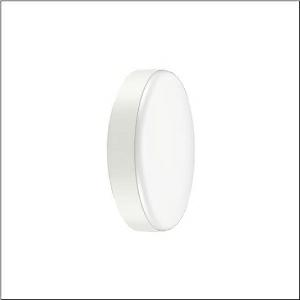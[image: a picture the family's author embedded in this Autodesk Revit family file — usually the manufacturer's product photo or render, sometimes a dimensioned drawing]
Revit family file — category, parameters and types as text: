
# Revit family: round_31_51wc10db44as
name_source: partatom
category: Lighting Fixtures
units: mm (PartAtom-declared; Revit-internal decimal feet)

## family parameters
Cut with Voids When Loaded = No
Host = Face
Light Source = No
Part Type = Normal
Room Calculation Point = No
Round Connector Dimension = Use Diameter
Shared = No

## types (1)
- Round 31 (1 x LED, 4400 lm, 35.5 W, 4000K)
    Apparent Load = 36 VA
    CIE Flux Codes = 44 75 94 94 100
    Color Rendering = 80
    Color Temperature = 4000K
    Default Elevation = 1800 mm
    Description = Round 31, wall and ceiling luminaire, primary optical cover: cover, of PC, opal, light emission: direct distribution, primary light characteristic: symmetric, installation type: surface-mounted, LED, rated luminous flux: 4.400lm, luminous efficacy: 124lm/W, light colour: 840, colour temperature: 4000K, control gear: DALI 2, with terminal, 3-pole, max. 2.5mm², mains connection: 220..240V, AC, 50/60Hz, rated input power: 35.5W, luminaire housing, of PC, traffic white (RAL 9016), diameter: 480mm, brightness and presence sensor, HF sensor, protection rating (complete): IP65, insulation class (complete): insulation class II (safety insulation), certification: CE, impact resistance: IK10, permissible operating ambient temperature: -20..+40°C, permissible storage temperature: -20..+60°C, packaging unit: 1 piece
    Height = 97 mm
    Lamp = 1 x LED
    Lamp Light Flux = 4400 lm
    Lamp Power = 35.5 W
    Lamp count = 1
    Length = 480 mm
    Luminous efficacy = 124 lm/W
    Manufacturer = Siteco
    ModVariant = No
    Model = 51WC10DB44AS
    Mounting Place = Ceiling
    Mounting Type = Surface mounted
    Number of Poles = 1
    OnlyDefault = Yes
    Power Factor = 1
    Product Name = Round 31
    Product group = wall and ceiling luminaire | ceiling mounted
    ProductGroupID = 305
    Protection Class = Protection class II
    Protection Degree = IP 65
    RLX_Detail_Level = 1
    RLX_Emergency_Light_Flux = 0 lm
    RLX_Emergency_Type = 0
    RLX_Emergency_Type_DB = No
    RlxData = <blob elided: 40957 chars, md5=95e477b4>
    Socket = socket
    Standby Power = 0 W
    System Light Flux = 4400 lm
    System Power = 36 W
    Type Comments = Product without accessories
    Type Image = l_1007188.jpg
    URL = http://relux.com
    VarID = ---
    Voltage = 0 V
    Weight = 0.00 kg
    Width = 0 mm  [stored 0 ft]

note: [stored X ft] marks values corroborated as IEEE doubles in the binary element streams (Revit-internal decimal feet)

## geometry (parser evidence)
native form markers: Blend x4, Sweep x14
no freeform markers — native parametric forms only
